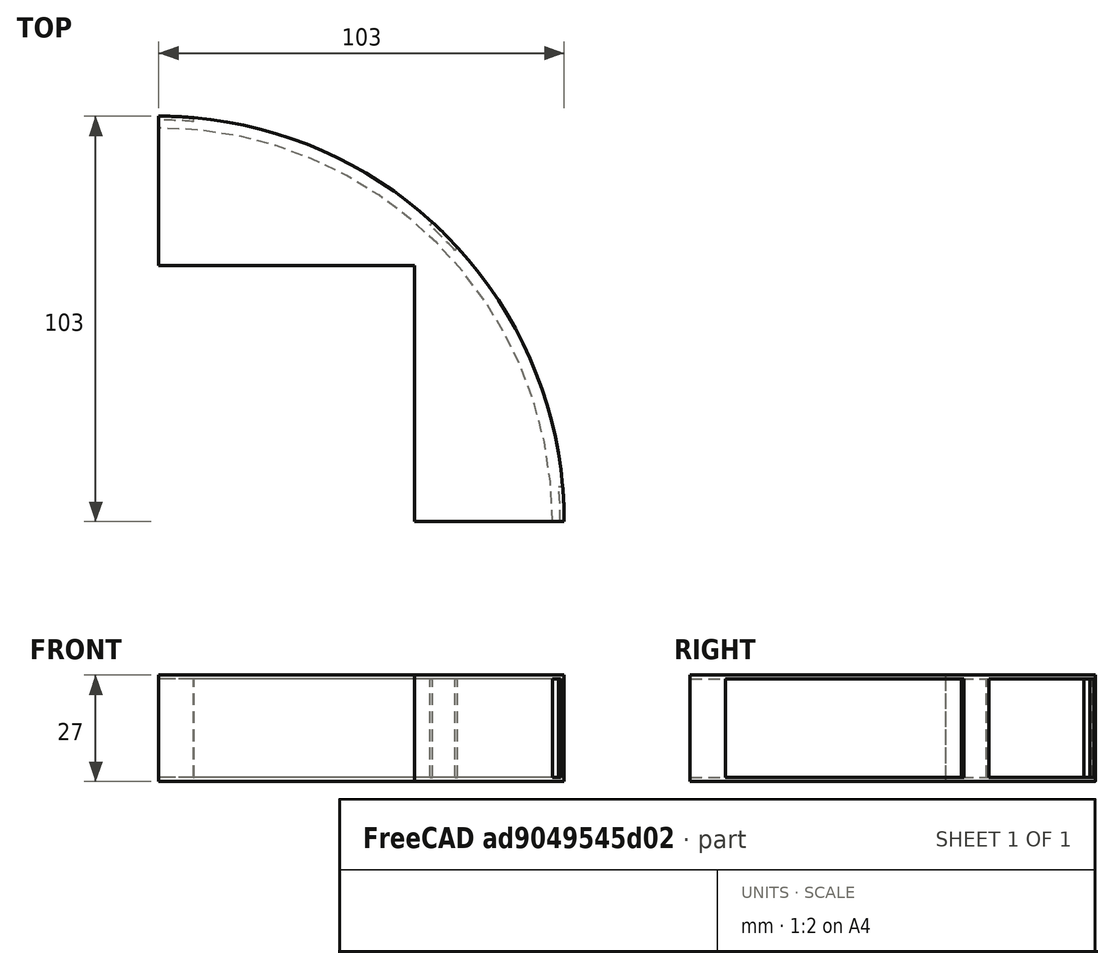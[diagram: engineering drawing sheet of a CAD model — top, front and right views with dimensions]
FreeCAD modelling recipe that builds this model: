
FCSTD DOCUMENT  (FreeCAD 0.17R13543 (Git))
Label: rahmenspanner
License: All rights reserved
LicenseURL: http://en.wikipedia.org/wiki/All_rights_reserved
objects: Part::Cylinder×9, Part::Cut×4, Part::MultiFuse×2, Part::Box×1
note: 16 computed .brp shape members not serialized (recipe doc carries the construction recipe); baked Part::Feature solids carry a one-line shape summary decoded from their .brp

FEATURE [Part::Cylinder] Cylinder  label="Zylinder"
  Angle = 90
  AttacherType = Attacher::AttachEngine3D
  Height = 25
  Radius = 100
FEATURE [Part::Cylinder] Cylinder001  label="Zylinder001"
  Angle = 90
  AttacherType = Attacher::AttachEngine3D
  Height = 1
  Placement = pos=(0,0,-1) rot=(0,0,1;0rad)
  Radius = 103
FEATURE [Part::Cylinder] Cylinder002  label="Zylinder002"
  Angle = 90
  AttacherType = Attacher::AttachEngine3D
  Height = 1
  Placement = pos=(0,0,25) rot=(0,0,1;0rad)
  Radius = 103
FEATURE [Part::Box] Box  label="Würfel"
  AttacherType = Attacher::AttachEngine3D
  Height = 27
  Length = 65
  Placement = pos=(0,0,-1) rot=(0,0,1;0rad)
  Width = 65
FEATURE [Part::MultiFuse] Fusion
  Shapes = -> [Cylinder,Cylinder001,Cylinder002]
FEATURE [Part::Cut] Cut
  Base = -> Fusion
  Tool = -> Box
FEATURE [Part::Cylinder] Cylinder003  label="Zylinder003"
  Angle = 5
  AttacherType = Attacher::AttachEngine3D
  Height = 27
  Placement = pos=(0,0,-1) rot=(0,0,1;0rad)
  Radius = 103
FEATURE [Part::Cylinder] Cylinder004  label="Zylinder004"
  Angle = 5
  AttacherType = Attacher::AttachEngine3D
  Height = 27
  Placement = pos=(0,0,-1) rot=(0,0,1;0rad)
  Radius = 102
FEATURE [Part::Cut] Cut001
  Base = -> Cylinder003
  Tool = -> Cylinder004
FEATURE [Part::Cylinder] Cylinder005  label="Zylinder005"
  Angle = 5
  AttacherType = Attacher::AttachEngine3D
  Height = 27
  Placement = pos=(0,0,-1) rot=(0,0,1;0rad)
  Radius = 102
FEATURE [Part::Cylinder] Cylinder006  label="Zylinder006"
  Angle = 5
  AttacherType = Attacher::AttachEngine3D
  Height = 27
  Placement = pos=(0,0,-1) rot=(0,0,1;0rad)
  Radius = 103
FEATURE [Part::Cut] Cut002
  Base = -> Cylinder006
  Placement = pos=(0,0,0) rot=(0,0,1;0.741765rad)
  Tool = -> Cylinder005
FEATURE [Part::Cylinder] Cylinder007  label="Zylinder007"
  Angle = 5
  AttacherType = Attacher::AttachEngine3D
  Height = 27
  Placement = pos=(0,0,-1) rot=(0,0,1;0rad)
  Radius = 103
FEATURE [Part::Cylinder] Cylinder008  label="Zylinder008"
  Angle = 5
  AttacherType = Attacher::AttachEngine3D
  Height = 27
  Placement = pos=(0,0,-1) rot=(0,0,1;0rad)
  Radius = 102
FEATURE [Part::Cut] Cut003
  Base = -> Cylinder007
  Placement = pos=(0,0,0) rot=(0,0,1;1.48353rad)
  Tool = -> Cylinder008
FEATURE [Part::MultiFuse] Fusion001
  Shapes = -> [Cut,Cut003,Cut001,Cut002]
